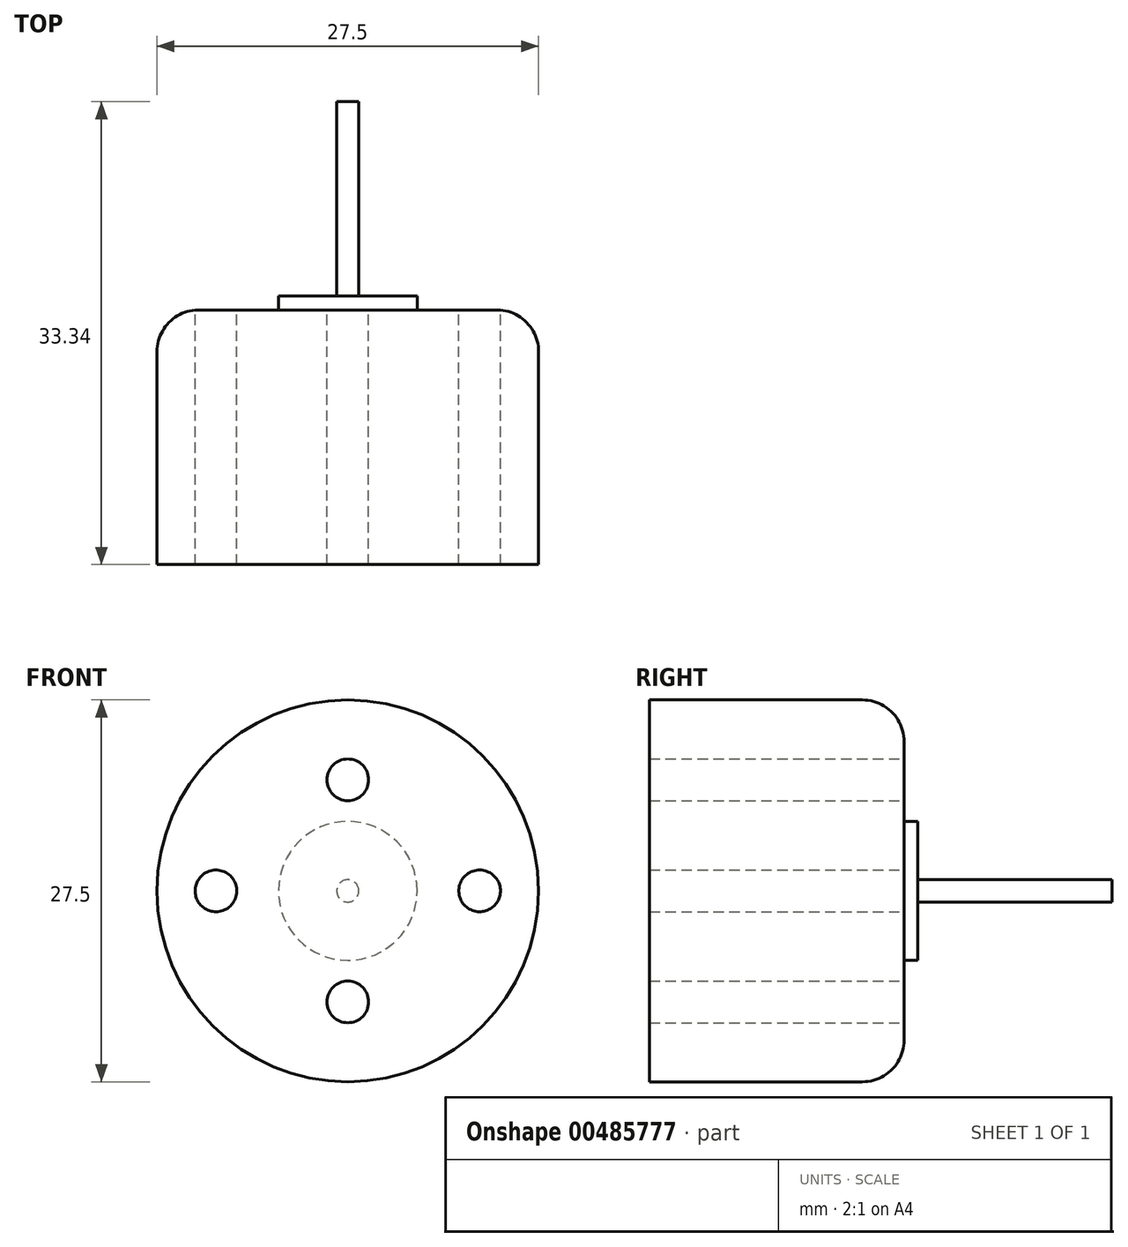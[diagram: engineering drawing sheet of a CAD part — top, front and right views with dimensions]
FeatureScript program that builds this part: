
annotation { "Feature Type Name" : "Feature", "Feature Type Description" : "" }
export const myFeature = defineFeature(function(context is Context, id is Id, definition is map)
    precondition{}
    {
        {
            var Q0;
            Q0=qCreatedBy(makeId("Front.planeOp"),FACE);
            var sketch = newSketch(context, id + "F0", { "sketchPlane" : qUnion([Q0])});
            skCircle(sketch, "E0", {"center": v(0, 0) * mm, "radius": 13.75 * mm});
            skCircle(sketch, "E1", {"center": v(0, 8) * mm, "radius": 1.5 * mm});
            skCircle(sketch, "E2.1.0", {"center": v(0, -8) * mm, "radius": 1.5 * mm});
            skCircle(sketch, "E3", {"center": v(-9.5, 0) * mm, "radius": 1.5 * mm});
            skCircle(sketch, "E4.1.0", {"center": v(9.5, 0) * mm, "radius": 1.5 * mm});
            skSolve(sketch);
        }
        {
            var Q0;
            Q0=makeQuery(id+"F0.imprint","IMPRINT",FACE,{"disambiguationData":[TD([[makeQuery(id+"F0.imprint","IMPRINT",EDGE,{"derivedFrom":sQuery(id+"F0.wireOp",EDGE,"E0")}),1.0]])]});
            extrude(context, id + "F1", {"entities" : qUnion([Q0]), "depth" : 18.34 * mm, "offsetDistance" : 25 * mm});
        }
        {
            var Q0;
            Q0=qCreatedBy(makeId("Front.planeOp"),FACE);
            var sketch = newSketch(context, id + "F2", { "sketchPlane" : qUnion([Q0])});
            skCircle(sketch, "E5", {"center": v(0, 0) * mm, "radius": 5 * mm});
            skSolve(sketch);
        }
        {
            var Q0;
            Q0=makeQuery(id+"F2.imprint","IMPRINT",FACE,{"disambiguationData":[TD([[makeQuery(id+"F2.imprint","IMPRINT",EDGE,{"derivedFrom":sQuery(id+"F2.wireOp",EDGE,"E5")}),1.0]])]});
            extrude(context, id + "F3", {"entities" : qUnion([Q0]), "operationType" : NewBodyOperationType.ADD, "oppositeDirection" : true, "depth" : 1 * mm, "offsetDistance" : 25 * mm});
        }
        {
            var Q0;
            Q0=qCreatedBy(makeId("Front.planeOp"),FACE);
            var sketch = newSketch(context, id + "F4", { "sketchPlane" : qUnion([Q0])});
            skCircle(sketch, "E6", {"center": v(0, 0) * mm, "radius": 0.8 * mm});
            skSolve(sketch);
        }
        {
            var Q0;
            Q0 = qSketchRegion(id + "F4", true);
            extrude(context, id + "F5", {"entities" : qUnion([Q0]), "operationType" : NewBodyOperationType.ADD, "oppositeDirection" : true, "depth" : 15 * mm, "offsetDistance" : 25 * mm});
        }
        {
            var Q0;
            Q0=makeQuery(id+"F1.opExtrude","CAP_EDGE",EDGE,{"disambiguationData":[OSD([sQuery(id+"F0.wireOp",EDGE,"E0")])],"isStart":true});
            fillet(context, id + "F6", {"entities" : qUnion([Q0]), "radius" : 3 * mm, "tangentPropagation" : true, "allowEdgeOverflow" : false});
        }
    });
